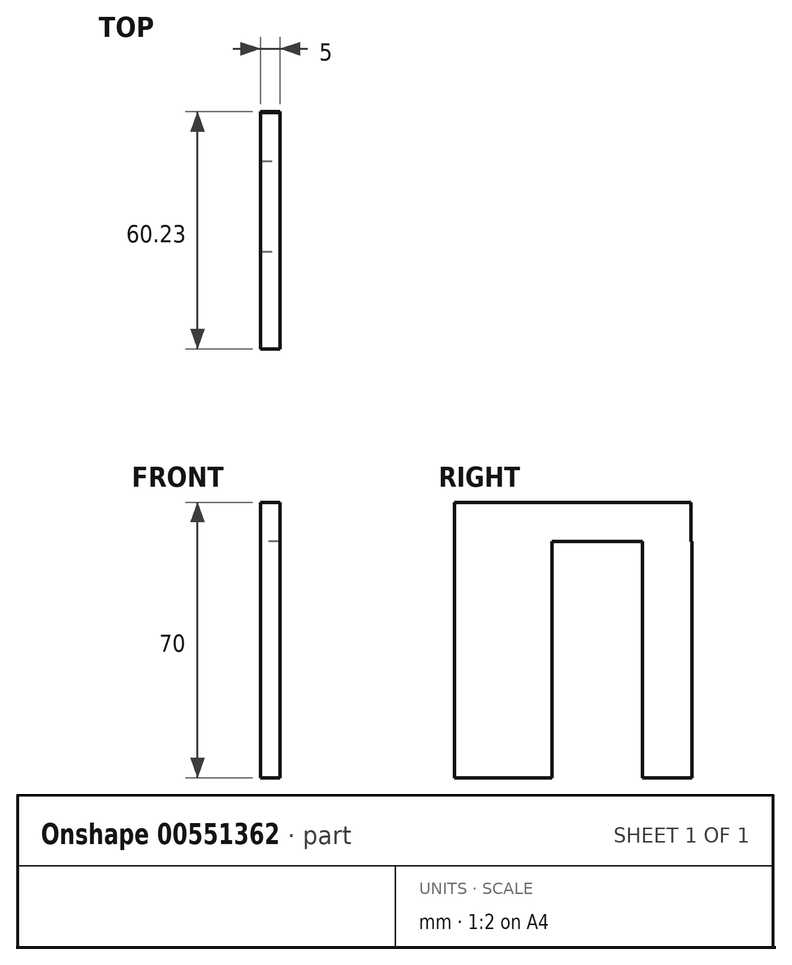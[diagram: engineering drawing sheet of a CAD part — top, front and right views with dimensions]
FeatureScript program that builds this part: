
annotation { "Feature Type Name" : "Feature", "Feature Type Description" : "" }
export const myFeature = defineFeature(function(context is Context, id is Id, definition is map)
    precondition{}
    {
        {
            var Q0;
            Q0=qCreatedBy(makeId("Right.planeOp"),FACE);
            var sketch = newSketch(context, id + "F0", { "sketchPlane" : qUnion([Q0])});
            skLineSegment(sketch, "E0.bottom", {"start": v(-64.4, 41) * mm, "end": v(-4.4, 41) * mm});
            skLineSegment(sketch, "E0.top", {"start": v(-64.4, -29) * mm, "end": v(-4.4, -29) * mm});
            skLineSegment(sketch, "E0.left", {"start": v(-64.4, 41) * mm, "end": v(-64.4, -29) * mm});
            skLineSegment(sketch, "E0.right", {"start": v(-4.4, 41) * mm, "end": v(-4.4, -29) * mm});
            skLineSegment(sketch, "E1.bottom", {"start": v(-4.16, -29) * mm, "end": v(-29.16, -29) * mm});
            skLineSegment(sketch, "E1.top", {"start": v(-4.16, 31) * mm, "end": v(-29.16, 31) * mm});
            skLineSegment(sketch, "E1.left", {"start": v(-4.16, -29) * mm, "end": v(-4.16, 31) * mm});
            skLineSegment(sketch, "E1.right", {"start": v(-29.16, -29) * mm, "end": v(-29.16, 31) * mm});
            skSolve(sketch);
        }
        {
            var Q0;
            Q0 = qSketchRegion(id + "F0", true);
            extrude(context, id + "F1", {"entities" : qUnion([Q0]), "depth" : 5 * mm, "offsetDistance" : 25 * mm});
        }
        {
            var Q0;
            Q0=makeQuery(id+"F1.opExtrude","CAP_FACE",FACE,{"disambiguationData":[OSD([sQuery(id+"F0.wireOp",EDGE,"E0.bottom"),sQuery(id+"F0.wireOp",EDGE,"E0.top"),sQuery(id+"F0.wireOp",EDGE,"E0.left"),sQuery(id+"F0.wireOp",EDGE,"E0.right"),sQuery(id+"F0.wireOp",EDGE,"E1.bottom")])],"isStart":false});
            var sketch = newSketch(context, id + "F2", { "sketchPlane" : qUnion([Q0])});
            skLineSegment(sketch, "E2.bottom", {"start": v(-16.68, -29) * mm, "end": v(-39.68, -29) * mm});
            skLineSegment(sketch, "E2.top", {"start": v(-16.68, 31) * mm, "end": v(-39.68, 31) * mm});
            skLineSegment(sketch, "E2.left", {"start": v(-16.68, -29) * mm, "end": v(-16.68, 31) * mm});
            skLineSegment(sketch, "E2.right", {"start": v(-39.68, -29) * mm, "end": v(-39.68, 31) * mm});
            skSolve(sketch);
        }
        {
            var Q0;
            Q0 = qSketchRegion(id + "F2", true);
            extrude(context, id + "F3", {"entities" : qUnion([Q0]), "operationType" : NewBodyOperationType.REMOVE, "oppositeDirection" : true, "depth" : 25 * mm, "offsetDistance" : 25 * mm});
        }
    });
